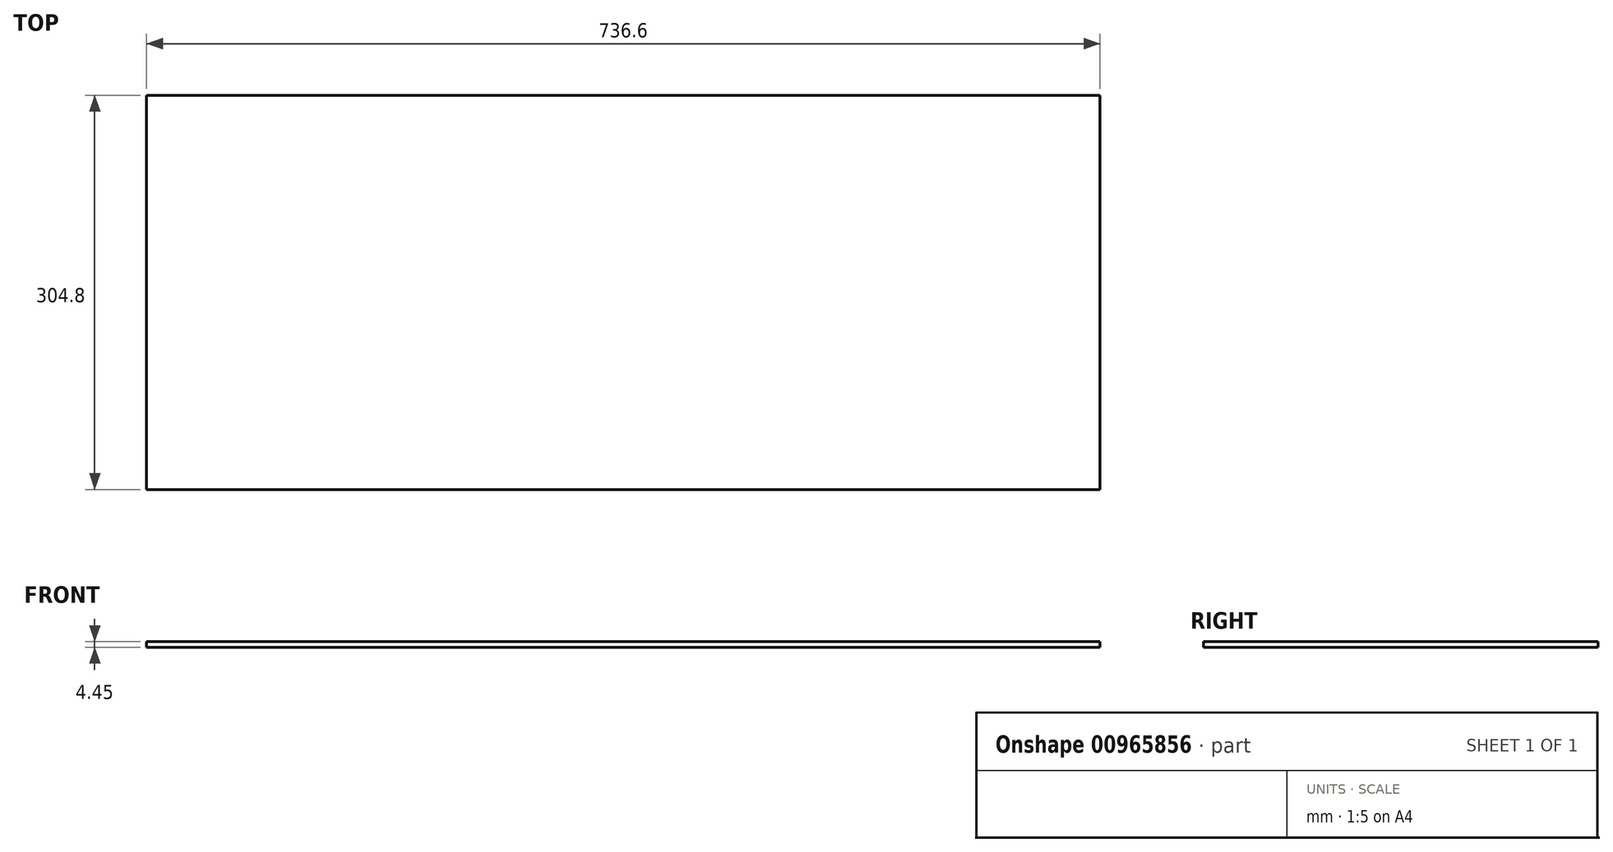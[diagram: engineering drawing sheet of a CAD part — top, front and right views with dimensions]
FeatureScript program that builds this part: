
annotation { "Feature Type Name" : "Feature", "Feature Type Description" : "" }
export const myFeature = defineFeature(function(context is Context, id is Id, definition is map)
    precondition{}
    {
        {
            var Q0;
            Q0=qCreatedBy(makeId("Top.planeOp"),FACE);
            var sketch = newSketch(context, id + "F0", { "sketchPlane" : qUnion([Q0])});
            skLineSegment(sketch, "E0.bottom", {"start": v(368.3, -152.4) * mm, "end": v(-368.3, -152.4) * mm});
            skLineSegment(sketch, "E0.top", {"start": v(368.3, 152.4) * mm, "end": v(-368.3, 152.4) * mm});
            skLineSegment(sketch, "E0.left", {"start": v(368.3, -152.4) * mm, "end": v(368.3, 152.4) * mm});
            skLineSegment(sketch, "E0.right", {"start": v(-368.3, -152.4) * mm, "end": v(-368.3, 152.4) * mm});
            skPoint(sketch, "E0.middle", {"position": v(0, 0) * mm});
            skSolve(sketch);
        }
        {
            var Q0;
            Q0=makeQuery(id+"F0.imprint","IMPRINT",FACE,{"disambiguationData":[TD([[makeQuery(id+"F0.imprint","IMPRINT",EDGE,{"derivedFrom":sQuery(id+"F0.wireOp",EDGE,"E0.bottom")}),-1.0]])]});
            extrude(context, id + "F1", {"entities" : qUnion([Q0]), "depth" : 4.45 * mm, "offsetDistance" : 25.4 * mm});
        }
    });
